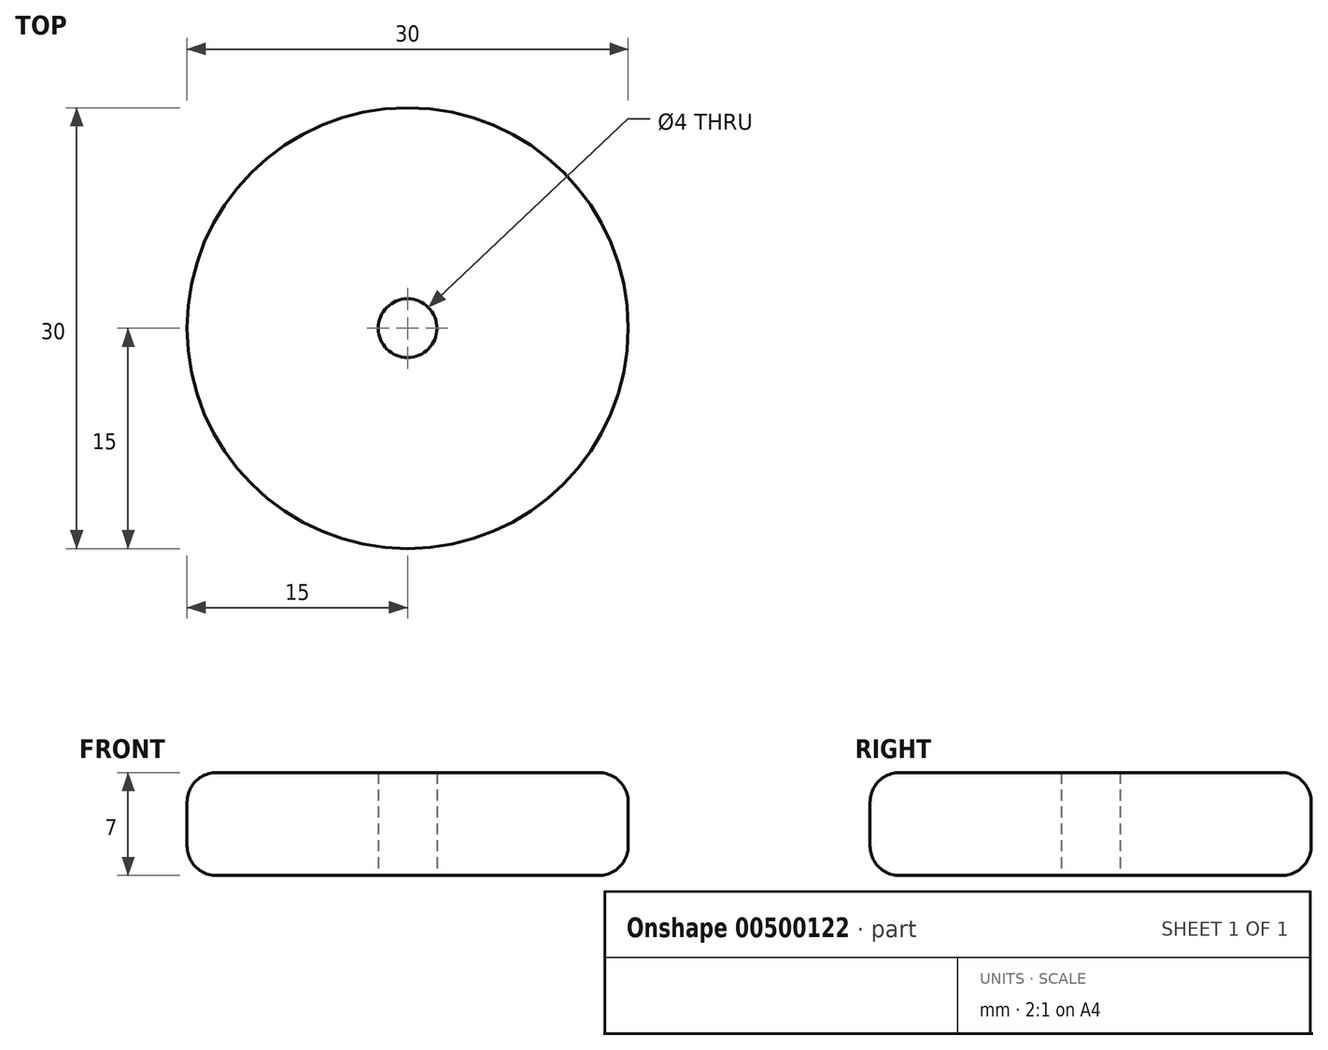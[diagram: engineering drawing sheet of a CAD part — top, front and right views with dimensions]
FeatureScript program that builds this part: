
annotation { "Feature Type Name" : "Feature", "Feature Type Description" : "" }
export const myFeature = defineFeature(function(context is Context, id is Id, definition is map)
    precondition{}
    {
        {
            var Q0;
            Q0=qCreatedBy(makeId("Top.planeOp"),FACE);
            var sketch = newSketch(context, id + "F0", { "sketchPlane" : qUnion([Q0])});
            skCircle(sketch, "E0", {"center": v(0, 0) * mm, "radius": 2 * mm});
            skCircle(sketch, "E1", {"center": v(0, 0) * mm, "radius": 15 * mm});
            skSolve(sketch);
        }
        {
            var Q0;
            Q0 = qSketchRegion(id + "F0", true);
            extrude(context, id + "F1", {"entities" : qUnion([Q0]), "depth" : 7 * mm, "offsetDistance" : 25 * mm});
        }
        {
            var Q0;
            Q0=makeQuery(id+"F1.opExtrude","CAP_EDGE",EDGE,{"disambiguationData":[OSD([sQuery(id+"F0.wireOp",EDGE,"E1")])],"isStart":false});
            fillet(context, id + "F2", {"entities" : qUnion([Q0]), "radius" : 2 * mm, "tangentPropagation" : true, "allowEdgeOverflow" : false});
        }
        {
            var Q0;
            Q0=makeQuery(id+"F1.opExtrude","CAP_EDGE",EDGE,{"disambiguationData":[OSD([sQuery(id+"F0.wireOp",EDGE,"E1")])],"isStart":true});
            fillet(context, id + "F3", {"entities" : qUnion([Q0]), "radius" : 2 * mm, "tangentPropagation" : true, "allowEdgeOverflow" : false});
        }
    });
